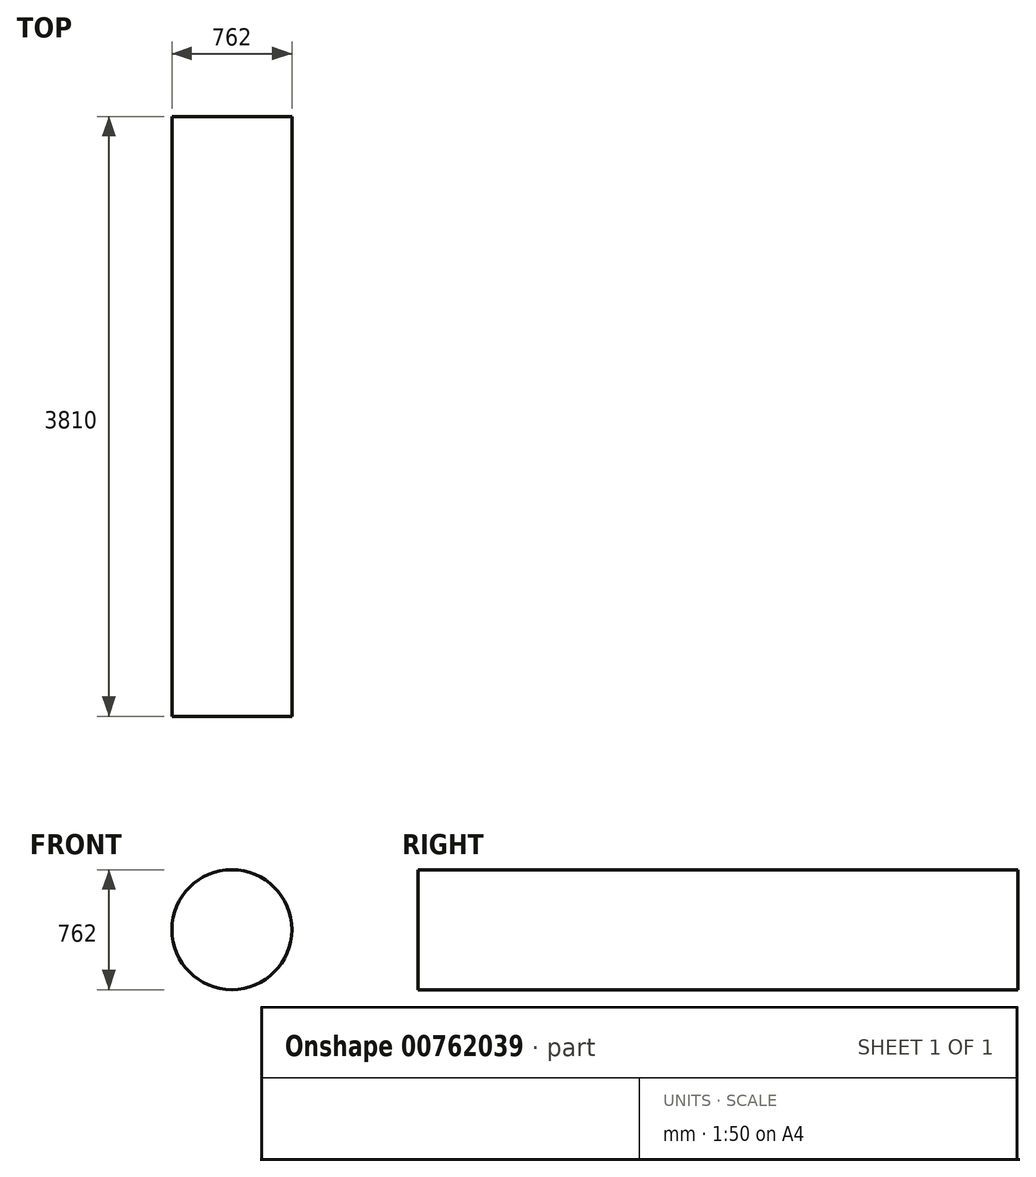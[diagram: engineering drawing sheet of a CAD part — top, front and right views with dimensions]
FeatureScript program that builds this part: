
annotation { "Feature Type Name" : "Feature", "Feature Type Description" : "" }
export const myFeature = defineFeature(function(context is Context, id is Id, definition is map)
    precondition{}
    {
        {
            var Q0;
            Q0=qCreatedBy(makeId("Front.planeOp"),FACE);
            var sketch = newSketch(context, id + "F0", { "sketchPlane" : qUnion([Q0])});
            skCircle(sketch, "E0", {"center": v(0, 0) * mm, "radius": 889 * mm});
            skCircle(sketch, "E1", {"center": v(0, 0) * mm, "radius": 381 * mm});
            skSolve(sketch);
        }
        {
            var Q0;
            Q0=makeQuery(id+"F0.imprint","IMPRINT",FACE,{"disambiguationData":[TD([[makeQuery(id+"F0.imprint","IMPRINT",EDGE,{"derivedFrom":sQuery(id+"F0.wireOp",EDGE,"E1")}),1.0]])]});
            extrude(context, id + "F1", {"entities" : qUnion([Q0]), "endBound" : BoundingType.SYMMETRIC, "depth" : 3810 * mm, "offsetDistance" : 25.4 * mm});
        }
    });
